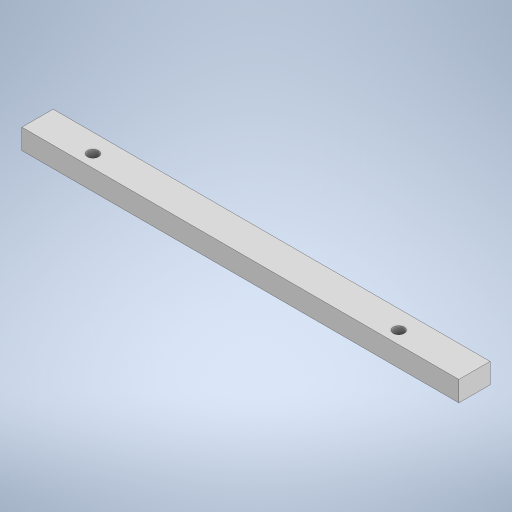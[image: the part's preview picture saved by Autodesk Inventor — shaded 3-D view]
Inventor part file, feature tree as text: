
AUTODESK INVENTOR PART (.ipt)
format: ipt  version: 2023 (Build 270158000, 158)  size: 254,976 bytes
history: native  units: in
note: dims shown in document units (in); Inventor stores cm internally (conversion verified against a paired STEP export)
features: sketch x5, extrude x4
ambient origin geometry x8: Origin, YZ Plane, XZ Plane, XY Plane, X Axis, Y Axis, Z Axis, Center Point
bodies: Solid1 (feature_tree)
feature tree (9):
  extrude  "Extrusion1"  Depth=0.3937in
  extrude  "Extrusion4"  Depth=0.1181in TaperAngle=0.0deg
  sketch  "Sketch7"  dims[d23=0.1693in d24=0.1693in]
  extrude  "Extrusion5"  Depth=0.1693in
  extrude  "Extrusion6"  Depth=0.1181in
  sketch  "Sketch1"  dims[d0=11.0236in d1=0.3937in]
  sketch  "Sketch6"  dims[d2=0.7874in d3=0.0in d21=0.1181in d22=0.0in]
  sketch  "Sketch8"  dims[d25=0.1181in d26=0.0in d27=0.2756in]
  sketch  "Sketch9"  dims[d28=0.2756in d29=0.3937in d30=0.0in d31=0.8108in d32=0.0025in d33=0.0295in d34=0.0148in]
